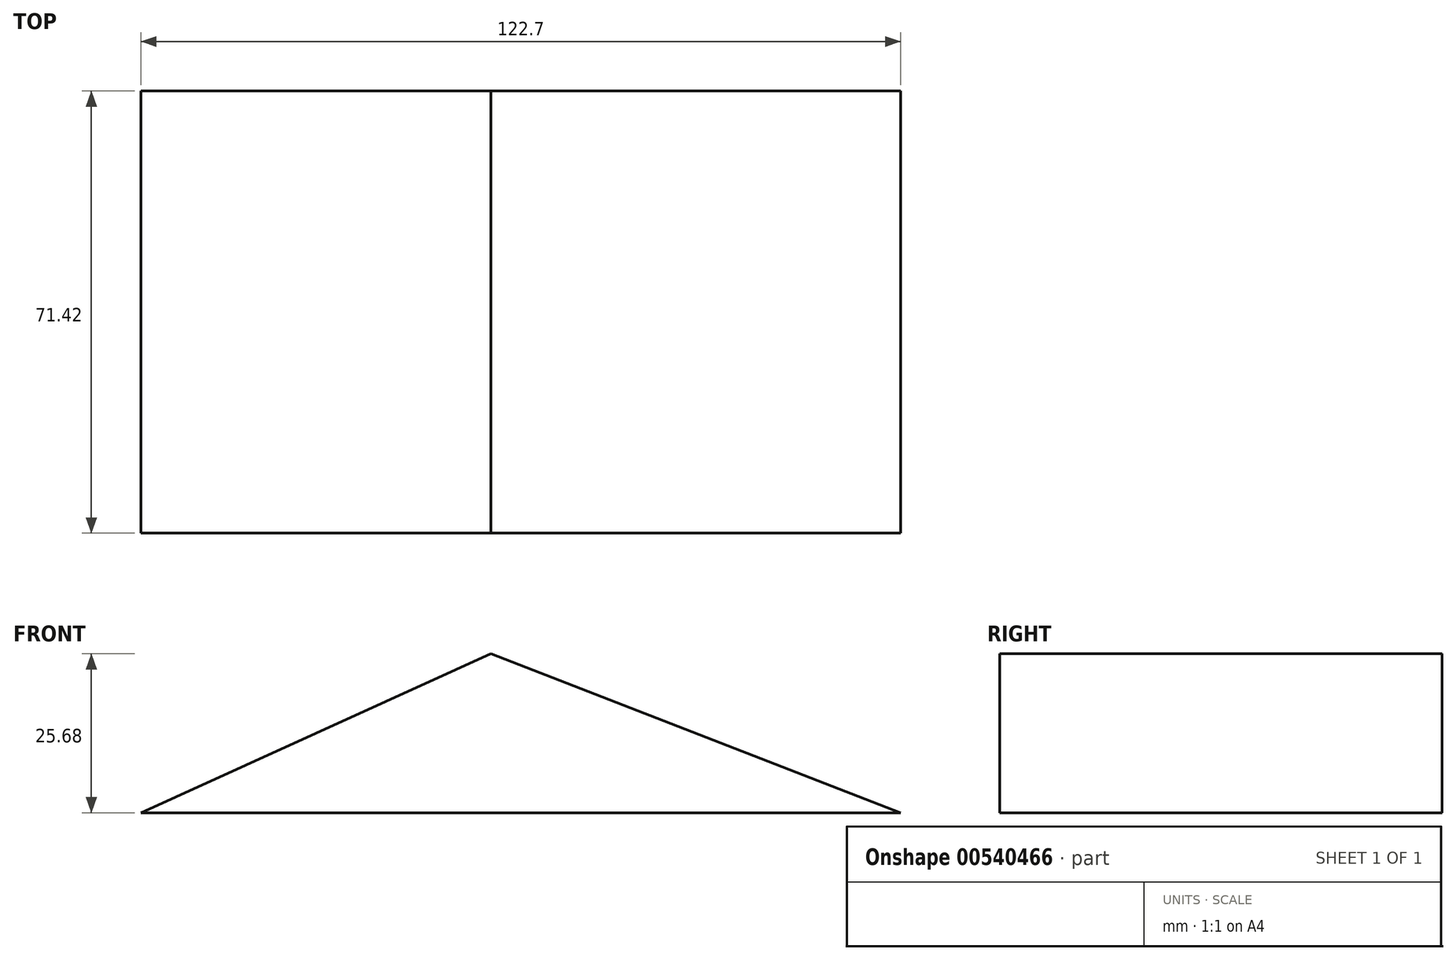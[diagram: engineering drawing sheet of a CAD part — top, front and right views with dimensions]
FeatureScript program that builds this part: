
annotation { "Feature Type Name" : "Feature", "Feature Type Description" : "" }
export const myFeature = defineFeature(function(context is Context, id is Id, definition is map)
    precondition{}
    {
        {
            var Q0;
            Q0=qCreatedBy(makeId("Front.planeOp"),FACE);
            var sketch = newSketch(context, id + "F0", { "sketchPlane" : qUnion([Q0])});
            skLineSegment(sketch, "E0", {"start": v(-47.68, 0) * mm, "end": v(75.02, 0) * mm});
            skLineSegment(sketch, "E1", {"start": v(-47.68, 0) * mm, "end": v(8.88, 25.68) * mm});
            skLineSegment(sketch, "E2", {"start": v(8.88, 25.68) * mm, "end": v(75.02, 0) * mm});
            skSolve(sketch);
        }
        {
            var Q0;
            Q0 = qSketchRegion(id + "F0", true);
            extrude(context, id + "F1", {"entities" : qUnion([Q0]), "depth" : 71.42 * mm, "offsetDistance" : 25.4 * mm});
        }
    });
